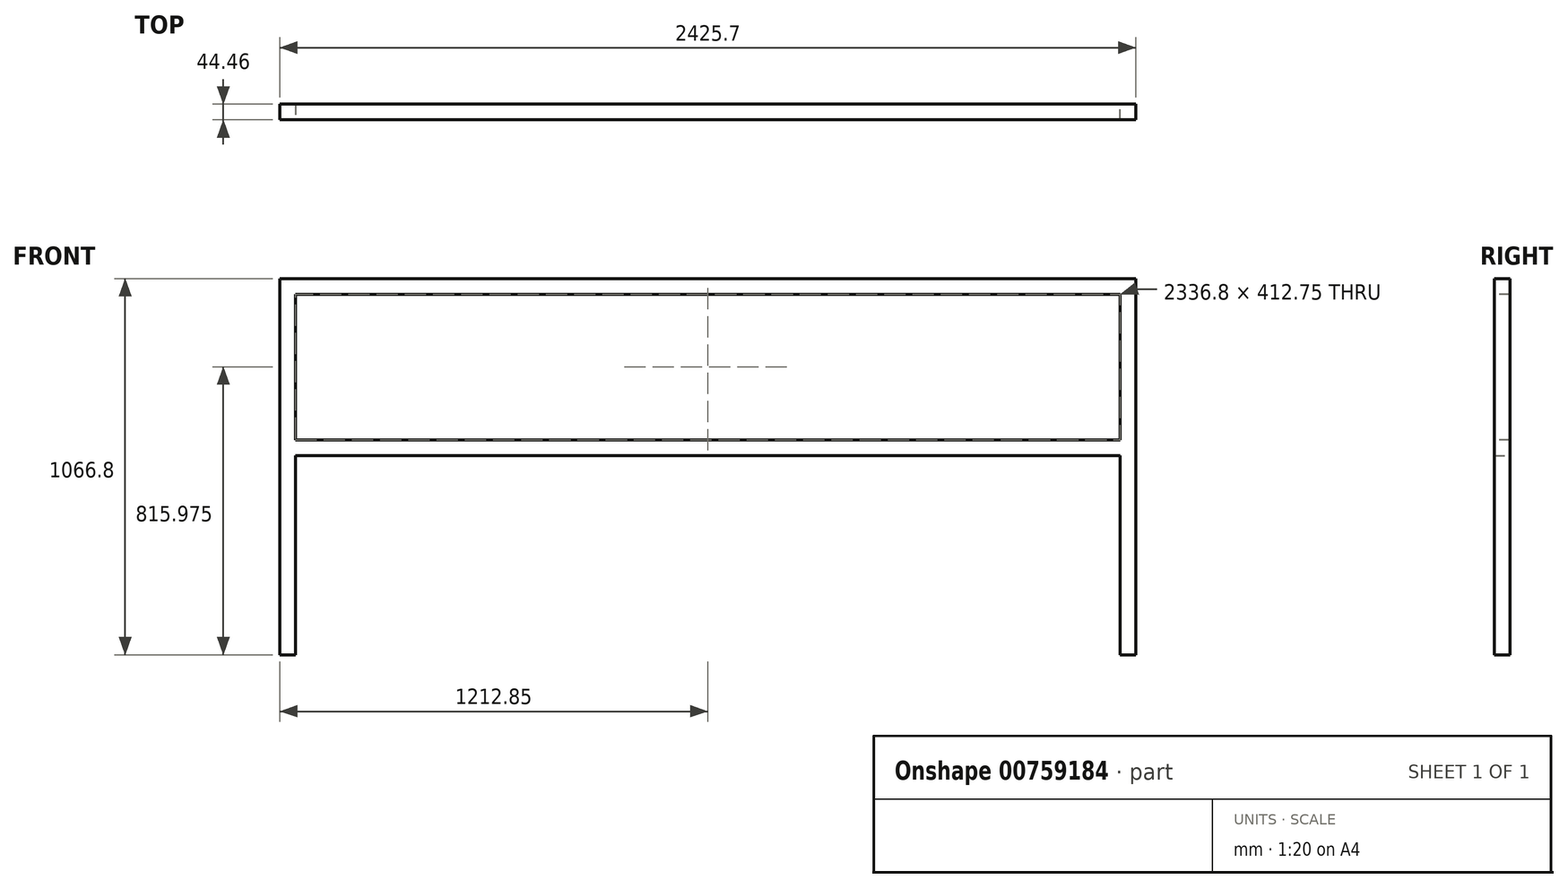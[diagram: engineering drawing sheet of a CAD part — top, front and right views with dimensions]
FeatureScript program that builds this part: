
annotation { "Feature Type Name" : "Feature", "Feature Type Description" : "" }
export const myFeature = defineFeature(function(context is Context, id is Id, definition is map)
    precondition{}
    {
        {
            var Q0;
            Q0=qCreatedBy(makeId("Front.planeOp"),FACE);
            var sketch = newSketch(context, id + "F0", { "sketchPlane" : qUnion([Q0])});
            skLineSegment(sketch, "E0", {"start": v(-1182.69, 0) * mm, "end": v(-1182.69, 1044.58) * mm});
            skLineSegment(sketch, "E1", {"start": v(-1182.69, 1044.58) * mm, "end": v(1198.56, 1044.58) * mm});
            skLineSegment(sketch, "E2", {"start": v(1198.56, 1044.58) * mm, "end": v(1198.56, 0) * mm});
            skLineSegment(sketch, "E3", {"start": v(-1182.69, 587.38) * mm, "end": v(1198.56, 587.38) * mm});
            skLineSegment(sketch, "E4.bottom", {"start": v(-1182.69, 609.6) * mm, "end": v(1198.56, 609.6) * mm});
            skLineSegment(sketch, "E4.top", {"start": v(-1182.69, 565.15) * mm, "end": v(1198.56, 565.15) * mm});
            skLineSegment(sketch, "E4.left", {"start": v(-1182.69, 609.6) * mm, "end": v(-1182.69, 565.15) * mm});
            skLineSegment(sketch, "E4.right", {"start": v(1198.56, 609.6) * mm, "end": v(1198.56, 565.15) * mm});
            skSolve(sketch);
        }
        {
            var Q0;
            Q0=qCreatedBy(makeId("Top.planeOp"),FACE);
            var sketch = newSketch(context, id + "F1", { "sketchPlane" : qUnion([Q0])});
            skLineSegment(sketch, "E5.bottom", {"start": v(-1204.91, 22.22) * mm, "end": v(-1160.46, 22.22) * mm});
            skLineSegment(sketch, "E5.top", {"start": v(-1204.91, -22.23) * mm, "end": v(-1160.46, -22.23) * mm});
            skLineSegment(sketch, "E5.left", {"start": v(-1204.91, 22.22) * mm, "end": v(-1204.91, -22.23) * mm});
            skLineSegment(sketch, "E5.right", {"start": v(-1160.46, 22.22) * mm, "end": v(-1160.46, -22.23) * mm});
            skPoint(sketch, "E5.middle", {"position": v(-1182.69, 0) * mm});
            skSolve(sketch);
        }
        {
            var Q0;
            Q0=makeQuery(id+"F1.imprint","IMPRINT",FACE,{"disambiguationData":[TD([[makeQuery(id+"F1.imprint","IMPRINT",EDGE,{"derivedFrom":sQuery(id+"F1.wireOp",EDGE,"E5.bottom")}),-1.0]])]});
            var Q1;
            Q1=sQuery(id+"F0.wireOp",EDGE,"E0");
            var Q2;
            Q2=sQuery(id+"F0.wireOp",EDGE,"dV9QwXlu-aOhN-80tf-FwMa-grVVV2uEPDh0");
            var Q3;
            Q3=sQuery(id+"F0.wireOp",EDGE,"E1");
            var Q4;
            Q4=sQuery(id+"F0.wireOp",EDGE,"Zx5w7UZY-6gg7-9vgH-Y3W4-xk5qzAeAtTve");
            var Q5;
            Q5=sQuery(id+"F0.wireOp",EDGE,"E2");
            sweep(context, id + "F2", {"profiles" : qUnion([Q0]), "path" : qUnion([Q1, Q2, Q3, Q4, Q5])});
        }
        {
            var Q0;
            {var subQ0=sQuery(id+"F0.wireOp",EDGE,"E3");Q0=makeQuery(id+"F0.imprint","IMPRINT",FACE,{"disambiguationData":[TD([[makeQuery(id+"F0.imprint","IMPRINT",EDGE,{"derivedFrom":subQ0}),1.0]])]});}
            var Q1;
            {var subQ0=sQuery(id+"F0.wireOp",EDGE,"E3");Q1=makeQuery(id+"F0.imprint","IMPRINT",FACE,{"disambiguationData":[TD([[makeQuery(id+"F0.imprint","IMPRINT",EDGE,{"derivedFrom":subQ0}),-1.0]])]});}
            extrude(context, id + "F3", {"entities" : qUnion([Q0, Q1]), "operationType" : NewBodyOperationType.ADD, "endBound" : BoundingType.SYMMETRIC, "depth" : 44.45 * mm, "offsetDistance" : 25.4 * mm});
        }
    });
